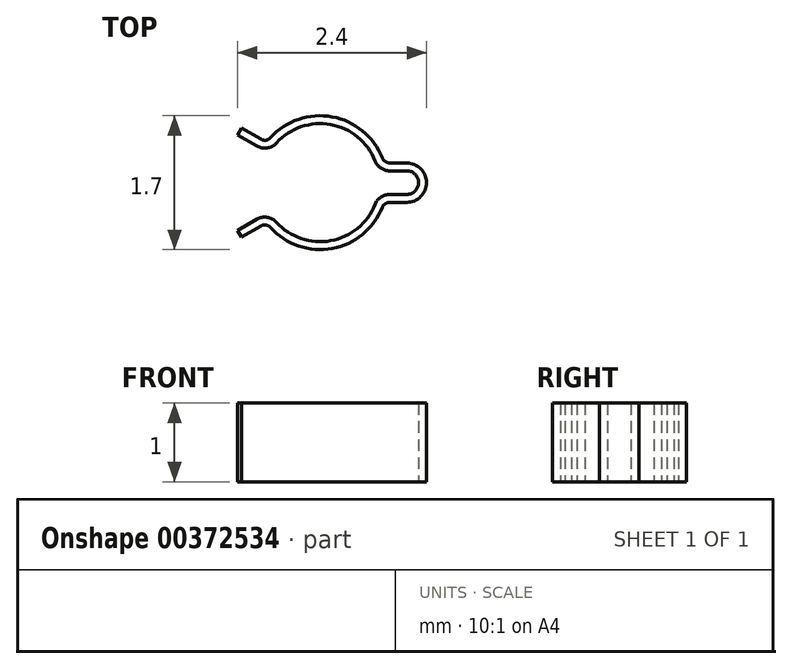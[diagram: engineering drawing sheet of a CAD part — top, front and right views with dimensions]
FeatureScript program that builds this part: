
annotation { "Feature Type Name" : "Feature", "Feature Type Description" : "" }
export const myFeature = defineFeature(function(context is Context, id is Id, definition is map)
    precondition{}
    {
        {
            var Q0;
            Q0=qCreatedBy(makeId("Top.planeOp"),FACE);
            var sketch = newSketch(context, id + "F0", { "sketchPlane" : qUnion([Q0])});
            skArc(sketch, "E0", {"start": v(0.7, 0.28) * mm, "mid": v(0.13, 0.74) * mm, "end": v(-0.56, 0.5) * mm});
            skArc(sketch, "E1", {"start": v(0.8, 0.31) * mm, "mid": v(0.15, 0.84) * mm, "end": v(-0.63, 0.57) * mm});
            skLineSegment(sketch, "E2", {"start": v(0, 0) * mm, "end": v(-1.2, 0.7) * mm, "construction": true});
            skLineSegment(sketch, "E3", {"start": v(0, 0) * mm, "end": v(-1.2, -0.7) * mm, "construction": true});
            skCircle(sketch, "E4", {"center": v(0, 0) * mm, "radius": 1.35 * mm, "construction": true});
            skArc(sketch, "E5", {"start": v(1.1, -0.25) * mm, "mid": v(1.35, 0) * mm, "end": v(1.1, 0.25) * mm});
            skArc(sketch, "E6", {"start": v(1.1, -0.15) * mm, "mid": v(1.25, 0) * mm, "end": v(1.1, 0.15) * mm});
            skLineSegment(sketch, "E7", {"start": v(1.1, 0.25) * mm, "end": v(0.88, 0.25) * mm});
            skLineSegment(sketch, "E8", {"start": v(1.1, 0.15) * mm, "end": v(0.88, 0.15) * mm});
            skLineSegment(sketch, "E9", {"start": v(1.1, -0.15) * mm, "end": v(0.88, -0.15) * mm});
            skLineSegment(sketch, "E10", {"start": v(1.1, -0.25) * mm, "end": v(0.88, -0.25) * mm});
            skPoint(sketch, "E11.visualSharp", {"position": v(0.81, 0.25) * mm});
            skArc(sketch, "E11.filletArc", {"start": v(0.8, 0.31) * mm, "mid": v(0.83, 0.27) * mm, "end": v(0.88, 0.25) * mm});
            skPoint(sketch, "E12.visualSharp", {"position": v(0.73, 0.15) * mm});
            skArc(sketch, "E12.filletArc", {"start": v(0.7, 0.28) * mm, "mid": v(0.77, 0.18) * mm, "end": v(0.88, 0.15) * mm});
            skPoint(sketch, "E13.visualSharp", {"position": v(0.81, -0.25) * mm});
            skArc(sketch, "E13.filletArc", {"start": v(0.88, -0.25) * mm, "mid": v(0.83, -0.27) * mm, "end": v(0.8, -0.31) * mm});
            skPoint(sketch, "E14.visualSharp", {"position": v(0.73, -0.15) * mm});
            skArc(sketch, "E14.filletArc", {"start": v(0.88, -0.15) * mm, "mid": v(0.77, -0.18) * mm, "end": v(0.7, -0.28) * mm});
            skLineSegment(sketch, "E15", {"start": v(1.35, 0) * mm, "end": v(-1.05, 0) * mm, "construction": true});
            skLineSegment(sketch, "E16", {"start": v(-1.05, -0.6) * mm, "end": v(-0.8, -0.46) * mm});
            skLineSegment(sketch, "E17", {"start": v(-1.05, 0.6) * mm, "end": v(-0.8, 0.46) * mm});
            skLineSegment(sketch, "E18", {"start": v(-1.05, 0.6) * mm, "end": v(-1, 0.7) * mm});
            skLineSegment(sketch, "E19", {"start": v(-1.05, -0.6) * mm, "end": v(-1, -0.7) * mm});
            skLineSegment(sketch, "E20", {"start": v(-1, -0.7) * mm, "end": v(-0.75, -0.55) * mm});
            skLineSegment(sketch, "E21", {"start": v(-1, 0.7) * mm, "end": v(-0.75, 0.55) * mm});
            skArc(sketch, "E22.trimOffspring", {"start": v(-0.56, -0.5) * mm, "mid": v(0.13, -0.74) * mm, "end": v(0.7, -0.28) * mm});
            skArc(sketch, "E23.trimOffspring", {"start": v(-0.63, -0.57) * mm, "mid": v(0.15, -0.84) * mm, "end": v(0.8, -0.31) * mm});
            skPoint(sketch, "E24.visualSharp", {"position": v(-0.68, 0.5) * mm});
            skArc(sketch, "E24.filletArc", {"start": v(-0.75, 0.55) * mm, "mid": v(-0.69, 0.54) * mm, "end": v(-0.63, 0.57) * mm});
            skPoint(sketch, "E25.visualSharp", {"position": v(-0.65, 0.38) * mm});
            skArc(sketch, "E25.filletArc", {"start": v(-0.8, 0.46) * mm, "mid": v(-0.67, 0.44) * mm, "end": v(-0.56, 0.5) * mm});
            skPoint(sketch, "E26.visualSharp", {"position": v(-0.68, -0.5) * mm});
            skArc(sketch, "E26.filletArc", {"start": v(-0.63, -0.57) * mm, "mid": v(-0.69, -0.54) * mm, "end": v(-0.75, -0.55) * mm});
            skPoint(sketch, "E27.visualSharp", {"position": v(-0.65, -0.38) * mm});
            skArc(sketch, "E27.filletArc", {"start": v(-0.56, -0.5) * mm, "mid": v(-0.67, -0.44) * mm, "end": v(-0.8, -0.46) * mm});
            skSolve(sketch);
        }
        {
            var Q0;
            Q0=makeQuery(id+"F0.imprint","IMPRINT",FACE,{"disambiguationData":[TD([[makeQuery(id+"F0.imprint","IMPRINT",EDGE,{"derivedFrom":sQuery(id+"F0.wireOp",EDGE,"E0")}),-1.0]])]});
            extrude(context, id + "F1", {"entities" : qUnion([Q0]), "depth" : 1 * mm});
        }
    });
